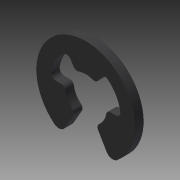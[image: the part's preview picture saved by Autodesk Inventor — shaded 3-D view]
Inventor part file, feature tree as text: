
AUTODESK INVENTOR PART (.ipt)
format: ipt  version: 2014 SP2 (Build 180246200, 246)  size: 129,536 bytes
history: native  units: in
note: dims shown in document units (in); Inventor stores cm internally (conversion verified against a paired STEP export)
features: other x7, extrude x1, sketch x1
ambient origin geometry x8: Origin, YZ Plane, XZ Plane, XY Plane, X Axis, Y Axis, Z Axis, Center Point
bodies: Solid1 (feature_tree)
feature tree (9):
  extrude  "Extrusion1"  [1 undecoded]
  other  "RR_XY"
  other  "RR_YZ"
  other  "RR_ZX"
  other  "RR_X"
  other  "RR_Y"
  other  "RR_Z"
  other  "RR_Center"
  sketch  "Sketch_1"  dims[d0=0.0435in d1=0.0in]
note: 1 required parameter value undecoded (feature->parameter linkage not recoverable at this tier; creation-order binding heuristic only, values carry confidence <= 0.55)
